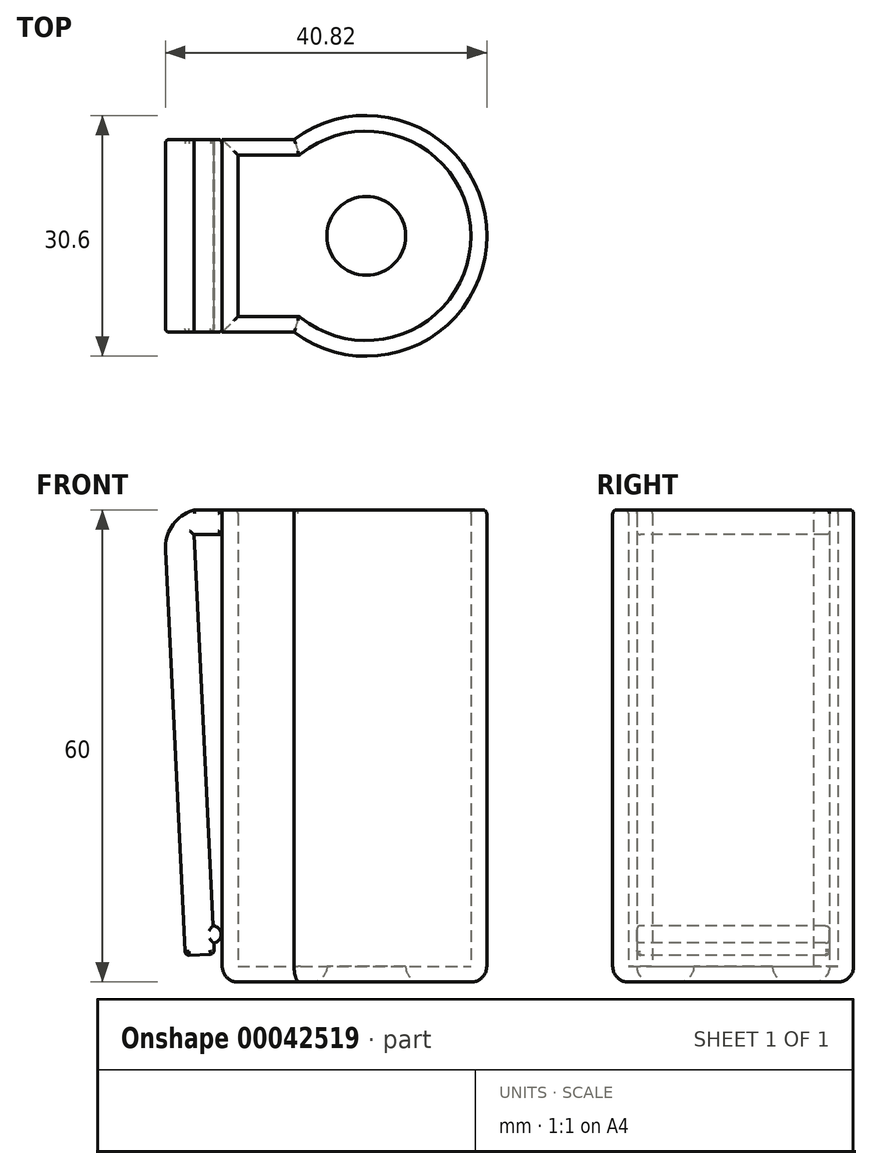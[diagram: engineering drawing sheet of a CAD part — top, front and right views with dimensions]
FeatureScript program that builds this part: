
annotation { "Feature Type Name" : "Feature", "Feature Type Description" : "" }
export const myFeature = defineFeature(function(context is Context, id is Id, definition is map)
    precondition{}
    {
        {
            var Q0;
            Q0=qCreatedBy(makeId("Top.planeOp"),FACE);
            var sketch = newSketch(context, id + "F0", { "sketchPlane" : qUnion([Q0])});
            skCircle(sketch, "E0", {"center": v(0, 0) * mm, "radius": 15.3 * mm});
            skPoint(sketch, "E1", {"position": v(-15.3, 0) * mm});
            skLineSegment(sketch, "E2", {"start": v(-15.3, 0) * mm, "end": v(-15.3, 12.25) * mm});
            skLineSegment(sketch, "E3", {"start": v(-15.3, 0) * mm, "end": v(-15.3, -12.25) * mm});
            skLineSegment(sketch, "E4", {"start": v(-15.3, -12.25) * mm, "end": v(-18.3, -12.25) * mm});
            skLineSegment(sketch, "E5", {"start": v(-18.3, -12.25) * mm, "end": v(-18.3, 12.25) * mm});
            skLineSegment(sketch, "E6", {"start": v(-15.3, 12.25) * mm, "end": v(-18.3, 12.25) * mm});
            skLineSegment(sketch, "E7", {"start": v(-15.3, 12.25) * mm, "end": v(-9.17, 12.25) * mm});
            skLineSegment(sketch, "E8", {"start": v(-15.3, -12.25) * mm, "end": v(-9.17, -12.25) * mm});
            skSolve(sketch);
        }
        {
            var Q0;
            Q0 = qSketchRegion(id + "F0", true);
            extrude(context, id + "F1", {"entities" : qUnion([Q0]), "depth" : 60 * mm});
        }
        {
            var Q0;
            Q0=makeQuery(id+"F1.opExtrude","CAP_FACE",FACE,{"disambiguationData":[OSD([sQuery(id+"F0.wireOp",EDGE,"E0")])],"isStart":false});
            shell(context, id + "F2", {"entities" : qUnion([Q0]), "thickness" : 2 * mm});
        }
        {
            var Q0;
            Q0=sQuery(id+"F0.wireOp",VERTEX,"E0.center");
            var Q1;
            Q1=makeQuery(id+"F1.opExtrude","SWEPT_BODY",BODY,{"disambiguationData":[OSD([sQuery(id+"F0.wireOp",EDGE,"E0")])]});
            hole(context, id + "F3", {"style" : HoleStyle.SIMPLE, "holeDiameter" : 10 * mm, "endStyle" : HoleEndStyle.THROUGH, "oppositeDirection" : true, "locations" : qUnion([Q0]), "scope" : qUnion([Q1])});
        }
        {
            var Q0;
            Q0=makeQuery(id+"F1.opExtrude","SWEPT_FACE",FACE,{"disambiguationData":[OSD([sQuery(id+"F0.wireOp",EDGE,"E4")])]});
            var sketch = newSketch(context, id + "F4", { "sketchPlane" : qUnion([Q0])});
            skLineSegment(sketch, "E9.bottom", {"start": v(-18.3, 60) * mm, "end": v(-21.9, 60) * mm});
            skLineSegment(sketch, "E9.top", {"start": v(-18.3, 56.83) * mm, "end": v(-21.9, 56.83) * mm});
            skLineSegment(sketch, "E9.left", {"start": v(-18.3, 60) * mm, "end": v(-18.3, 56.83) * mm});
            skLineSegment(sketch, "E9.right", {"start": v(-21.9, 60) * mm, "end": v(-21.9, 56.83) * mm});
            skLineSegment(sketch, "E10", {"start": v(-21.9, 56.83) * mm, "end": v(-19.3, 3.58) * mm});
            skLineSegment(sketch, "E11", {"start": v(-21.9, 60) * mm, "end": v(-25.69, 58.42) * mm});
            skPoint(sketch, "E11.endSnap0", {"position": v(-21.9, 58.42) * mm});
            skLineSegment(sketch, "E12", {"start": v(-25.69, 58.42) * mm, "end": v(-23, 3.4) * mm});
            skLineSegment(sketch, "E13", {"start": v(-23, 3.4) * mm, "end": v(-19.3, 3.58) * mm});
            skArc(sketch, "E14", {"start": v(-19.37, 4.95) * mm, "mid": v(-18.44, 6.1) * mm, "end": v(-19.47, 7.16) * mm});
            skSolve(sketch);
        }
        {
            var Q0;
            Q0 = qSketchRegion(id + "F4", true);
            extrude(context, id + "F5", {"entities" : qUnion([Q0]), "oppositeDirection" : true, "depth" : 24.5 * mm});
        }
        {
            var Q0;
            Q0=makeQuery(id+"F5.opExtrude","SWEPT_EDGE",EDGE,{"disambiguationData":[OSD([sQuery(id+"F4.wireOp",EDGE,"E11"),sQuery(id+"F4.wireOp",EDGE,"E12")])]});
            fillet(context, id + "F6", {"entities" : qUnion([Q0]), "radius" : 5 * mm, "tangentPropagation" : true, "allowEdgeOverflow" : false});
        }
        {
            var Q0;
            Q0=makeQuery(id+"F1.opExtrude","CAP_FACE",FACE,{"disambiguationData":[OSD([sQuery(id+"F0.wireOp",EDGE,"E0"),sQuery(id+"F0.wireOp",EDGE,"E4"),sQuery(id+"F0.wireOp",EDGE,"E5"),sQuery(id+"F0.wireOp",EDGE,"E6"),sQuery(id+"F0.wireOp",EDGE,"E7"),sQuery(id+"F0.wireOp",EDGE,"E8")])],"isStart":true});
            fillet(context, id + "F7", {"entities" : qUnion([Q0]), "radius" : 2 * mm, "tangentPropagation" : true, "allowEdgeOverflow" : false});
        }
        {
            var Q0;
            Q0=makeQuery(id+"F5.opExtrude","CAP_FACE",FACE,{"disambiguationData":[OSD([sQuery(id+"F4.wireOp",EDGE,"E9.bottom"),sQuery(id+"F4.wireOp",EDGE,"E9.top"),sQuery(id+"F4.wireOp",EDGE,"E9.left"),sQuery(id+"F4.wireOp",EDGE,"E10"),sQuery(id+"F4.wireOp",EDGE,"E11"),sQuery(id+"F4.wireOp",EDGE,"E12"),sQuery(id+"F4.wireOp",EDGE,"E13"),sQuery(id+"F4.wireOp",EDGE,"E14")])],"isStart":true});
            fillet(context, id + "F8", {"entities" : qUnion([Q0]), "radius" : 0.5 * mm, "tangentPropagation" : true, "allowEdgeOverflow" : false});
        }
        {
            var Q0;
            Q0=makeQuery(id+"F5.opExtrude","CAP_FACE",FACE,{"disambiguationData":[OSD([sQuery(id+"F4.wireOp",EDGE,"E9.bottom"),sQuery(id+"F4.wireOp",EDGE,"E9.top"),sQuery(id+"F4.wireOp",EDGE,"E9.left"),sQuery(id+"F4.wireOp",EDGE,"E10"),sQuery(id+"F4.wireOp",EDGE,"E11"),sQuery(id+"F4.wireOp",EDGE,"E12"),sQuery(id+"F4.wireOp",EDGE,"E13"),sQuery(id+"F4.wireOp",EDGE,"E14")])],"isStart":false});
            fillet(context, id + "F9", {"entities" : qUnion([Q0]), "radius" : 0.5 * mm, "tangentPropagation" : true, "allowEdgeOverflow" : false});
        }
        {
            var Q0;
            Q0=makeQuery(id+"F5.opExtrude","SWEPT_FACE",FACE,{"disambiguationData":[OSD([sQuery(id+"F4.wireOp",EDGE,"E13")])]});
            fillet(context, id + "F10", {"entities" : qUnion([Q0]), "radius" : 0.5 * mm, "tangentPropagation" : true, "allowEdgeOverflow" : false});
        }
        {
            var Q0;
            Q0=makeQuery(id+"F1.opExtrude","CAP_EDGE",EDGE,{"disambiguationData":[OSD([sQuery(id+"F0.wireOp",EDGE,"E6"),sQuery(id+"F0.wireOp",EDGE,"E7")])],"isStart":false});
            var Q1;
            {var subQ0=sQuery(id+"F0.wireOp",EDGE,"E6");var subQ1=sQuery(id+"F0.wireOp",EDGE,"E7");Q1=makeQuery(id+"F2.opShell","OFFSET_EDGE",EDGE,{"disambiguationData":[OSD([subQ0,subQ1]),TDD([makeQuery(id+"F1.opExtrude","CAP_EDGE",EDGE,{"disambiguationData":[OSD([subQ0,subQ1])],"isStart":false})])]});}
            var Q2;
            {var subQ0=sQuery(id+"F0.wireOp",EDGE,"E5");Q2=makeQuery(id+"F2.opShell","OFFSET_EDGE",EDGE,{"disambiguationData":[OSD([subQ0]),TDD([makeQuery(id+"F1.opExtrude","CAP_EDGE",EDGE,{"disambiguationData":[OSD([subQ0])],"isStart":false})])]});}
            var Q3;
            {var subQ0=sQuery(id+"F0.wireOp",EDGE,"E4");var subQ1=sQuery(id+"F0.wireOp",EDGE,"E8");Q3=makeQuery(id+"F2.opShell","OFFSET_EDGE",EDGE,{"disambiguationData":[OSD([subQ0,subQ1]),TDD([makeQuery(id+"F1.opExtrude","CAP_EDGE",EDGE,{"disambiguationData":[OSD([subQ0,subQ1])],"isStart":false})])]});}
            var Q4;
            Q4=makeQuery(id+"F1.opExtrude","CAP_EDGE",EDGE,{"disambiguationData":[OSD([sQuery(id+"F0.wireOp",EDGE,"E4"),sQuery(id+"F0.wireOp",EDGE,"E8")])],"isStart":false});
            fillet(context, id + "F11", {"entities" : qUnion([Q0, Q1, Q2, Q3, Q4]), "radius" : 0.5 * mm, "tangentPropagation" : true, "allowEdgeOverflow" : false});
        }
        {
            var Q0;
            Q0=makeQuery(id+"F1.opExtrude","CAP_EDGE",EDGE,{"disambiguationData":[OSD([sQuery(id+"F0.wireOp",EDGE,"E0")])],"isStart":false});
            var Q1;
            {var subQ0=sQuery(id+"F0.wireOp",EDGE,"E0");Q1=makeQuery(id+"F2.opShell","OFFSET_EDGE",EDGE,{"disambiguationData":[OSD([subQ0]),TDD([makeQuery(id+"F1.opExtrude","CAP_EDGE",EDGE,{"disambiguationData":[OSD([subQ0])],"isStart":false})])]});}
            fillet(context, id + "F12", {"entities" : qUnion([Q0, Q1]), "radius" : 0.5 * mm, "tangentPropagation" : true, "allowEdgeOverflow" : false});
        }
    });
